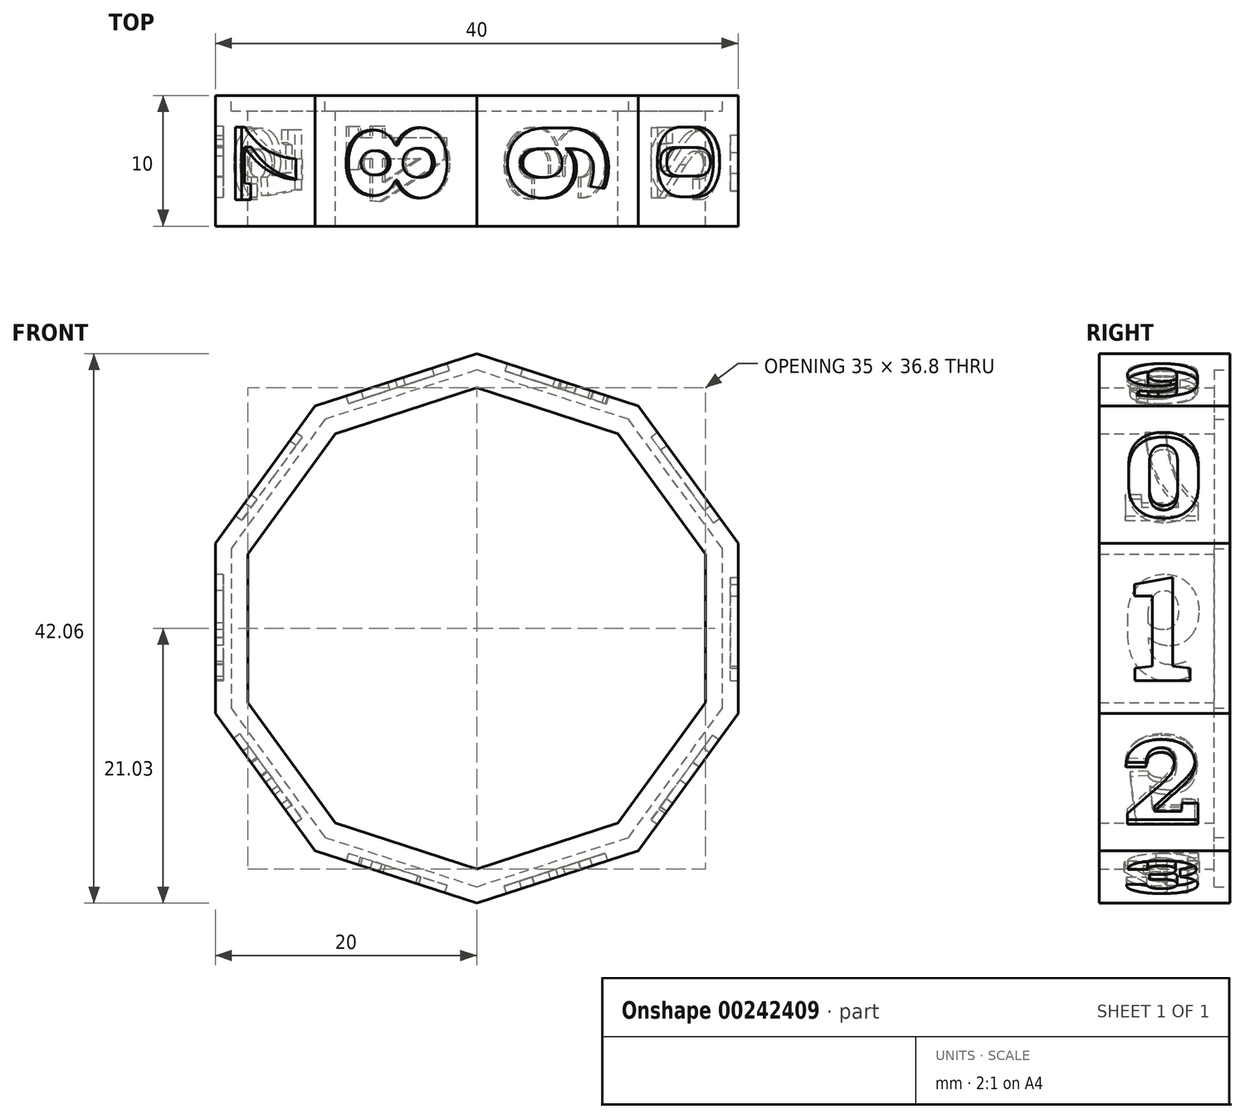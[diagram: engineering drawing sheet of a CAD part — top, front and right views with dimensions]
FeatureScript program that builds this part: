
annotation { "Feature Type Name" : "Feature", "Feature Type Description" : "" }
export const myFeature = defineFeature(function(context is Context, id is Id, definition is map)
    precondition{}
    {
        {
            var Q0;
            Q0=qCreatedBy(makeId("Front.planeOp"),FACE);
            var sketch = newSketch(context, id + "F0", { "sketchPlane" : qUnion([Q0])});
            skCircle(sketch, "E0.cCircle", {"center": v(0, 0) * mm, "radius": 20 * mm, "construction": true});
            skLineSegment(sketch, "E0.0", {"start": v(20, 6.5) * mm, "end": v(20, -6.5) * mm});
            skLineSegment(sketch, "E0.1", {"start": v(20, -6.5) * mm, "end": v(12.36, -17.01) * mm});
            skLineSegment(sketch, "E0.2", {"start": v(12.36, -17.01) * mm, "end": v(0, -21.03) * mm});
            skLineSegment(sketch, "E0.3", {"start": v(0, -21.03) * mm, "end": v(-12.36, -17.01) * mm});
            skLineSegment(sketch, "E0.4", {"start": v(-12.36, -17.01) * mm, "end": v(-20, -6.5) * mm});
            skLineSegment(sketch, "E0.5", {"start": v(-20, -6.5) * mm, "end": v(-20, 6.5) * mm});
            skLineSegment(sketch, "E0.6", {"start": v(-20, 6.5) * mm, "end": v(-12.36, 17.01) * mm});
            skLineSegment(sketch, "E0.7", {"start": v(-12.36, 17.01) * mm, "end": v(0, 21.03) * mm});
            skLineSegment(sketch, "E0.8", {"start": v(0, 21.03) * mm, "end": v(12.36, 17.01) * mm});
            skLineSegment(sketch, "E0.9", {"start": v(12.36, 17.01) * mm, "end": v(20, 6.5) * mm});
            skPoint(sketch, "E0.0.midPoint", {"position": v(20, 0) * mm});
            skSolve(sketch);
        }
        {
            var Q0;
            Q0=makeQuery(id+"F0.imprint","IMPRINT",FACE,{"disambiguationData":[TD([[makeQuery(id+"F0.imprint","IMPRINT",EDGE,{"derivedFrom":sQuery(id+"F0.wireOp",EDGE,"E0.0")}),-1.0]])]});
            extrude(context, id + "F1", {"entities" : qUnion([Q0]), "depth" : 10 * mm});
        }
        {
            var Q0;
            Q0=makeQuery(id+"F1.opExtrude","CAP_FACE",FACE,{"disambiguationData":[OSD([sQuery(id+"F0.wireOp",EDGE,"E0.0"),sQuery(id+"F0.wireOp",EDGE,"E0.1"),sQuery(id+"F0.wireOp",EDGE,"E0.2"),sQuery(id+"F0.wireOp",EDGE,"E0.3"),sQuery(id+"F0.wireOp",EDGE,"E0.4"),sQuery(id+"F0.wireOp",EDGE,"E0.5"),sQuery(id+"F0.wireOp",EDGE,"E0.6"),sQuery(id+"F0.wireOp",EDGE,"E0.7"),sQuery(id+"F0.wireOp",EDGE,"E0.8"),sQuery(id+"F0.wireOp",EDGE,"E0.9")])],"isStart":false});
            var Q1;
            Q1=makeQuery(id+"F1.opExtrude","SWEPT_BODY",BODY,{"disambiguationData":[OSD([sQuery(id+"F0.wireOp",EDGE,"E0.0"),sQuery(id+"F0.wireOp",EDGE,"E0.1"),sQuery(id+"F0.wireOp",EDGE,"E0.2"),sQuery(id+"F0.wireOp",EDGE,"E0.3"),sQuery(id+"F0.wireOp",EDGE,"E0.4"),sQuery(id+"F0.wireOp",EDGE,"E0.5"),sQuery(id+"F0.wireOp",EDGE,"E0.6"),sQuery(id+"F0.wireOp",EDGE,"E0.7"),sQuery(id+"F0.wireOp",EDGE,"E0.8"),sQuery(id+"F0.wireOp",EDGE,"E0.9")])]});
            shell(context, id + "F2", {"entities" : qUnion([Q0]), "parts" : qUnion([Q1]), "thickness" : 2.5 * mm});
        }
        {
            var Q0;
            Q0=makeQuery(id+"F2.opShell","OFFSET_FACE",FACE,{"disambiguationData":[OSD([sQuery(id+"F0.wireOp",EDGE,"E0.0"),sQuery(id+"F0.wireOp",EDGE,"E0.1"),sQuery(id+"F0.wireOp",EDGE,"E0.2"),sQuery(id+"F0.wireOp",EDGE,"E0.3"),sQuery(id+"F0.wireOp",EDGE,"E0.4"),sQuery(id+"F0.wireOp",EDGE,"E0.5"),sQuery(id+"F0.wireOp",EDGE,"E0.6"),sQuery(id+"F0.wireOp",EDGE,"E0.7"),sQuery(id+"F0.wireOp",EDGE,"E0.8"),sQuery(id+"F0.wireOp",EDGE,"E0.9")])]});
            extrude(context, id + "F3", {"entities" : qUnion([Q0]), "operationType" : NewBodyOperationType.REMOVE, "endBound" : BoundingType.THROUGH_ALL, "oppositeDirection" : true, "depth" : 25 * mm});
        }
        {
            var Q0;
            Q0=makeQuery(id+"F1.opExtrude","SWEPT_FACE",FACE,{"disambiguationData":[OSD([sQuery(id+"F0.wireOp",EDGE,"E0.0")])]});
            var sketch = newSketch(context, id + "F4", { "sketchPlane" : qUnion([Q0])});
            skText(sketch, "E1", { "text": "1", "fontName": "RobotoSlab-Bold.ttf"});
            skPoint(sketch, "E2", {"position": v(-5, 0) * mm});
            skPoint(sketch, "E3", {"position": v(-5, 6.5) * mm});
            skLineSegment(sketch, "E4", {"start": v(-5, 15.06) * mm, "end": v(-5, -15.22) * mm, "construction": true});
            skLineSegment(sketch, "E5", {"start": v(0, 0) * mm, "end": v(-19.55, 0) * mm, "construction": true});
            skPoint(sketch, "E5.endSnap0", {"position": v(-10, 0) * mm});
            const initialGuessF4  = {"E1": [-0.00764, -0.004, 1, 0, 0.008]};
            skSetInitialGuess(sketch, initialGuessF4);
            skSolve(sketch);
        }
        {
            var Q0;
            Q0=qCreatedBy(makeId("Right.planeOp"),FACE);
            var sketch = newSketch(context, id + "F5", { "sketchPlane" : qUnion([Q0])});
            skLineSegment(sketch, "E6", {"start": v(-30.34, 0) * mm, "end": v(47.05, 0) * mm, "construction": true});
            skSolve(sketch);
        }
        {
            var Q0;
            Q0=makeQuery(id+"F1.opExtrude","SWEPT_FACE",FACE,{"disambiguationData":[OSD([sQuery(id+"F0.wireOp",EDGE,"E0.1")])]});
            var sketch = newSketch(context, id + "F6", { "sketchPlane" : qUnion([Q0])});
            skText(sketch, "E7", { "text": "2", "fontName": "RobotoSlab-Bold.ttf"});
            skPoint(sketch, "E8", {"position": v(-5, 0) * mm});
            skPoint(sketch, "E9", {"position": v(-5, 6.5) * mm});
            skLineSegment(sketch, "E10", {"start": v(-5, 34.53) * mm, "end": v(-5, -39.22) * mm, "construction": true});
            const initialGuessF6  = {"E7": [-0.00823, -0.004, 1, 0, 0.008]};
            skSetInitialGuess(sketch, initialGuessF6);
            skSolve(sketch);
        }
        {
            var Q0;
            Q0=makeQuery(id+"F1.opExtrude","SWEPT_FACE",FACE,{"disambiguationData":[OSD([sQuery(id+"F0.wireOp",EDGE,"E0.2")])]});
            var sketch = newSketch(context, id + "F7", { "sketchPlane" : qUnion([Q0])});
            skText(sketch, "E11", { "text": "3", "fontName": "RobotoSlab-Bold.ttf"});
            skPoint(sketch, "E12", {"position": v(6.5, 5) * mm});
            skLineSegment(sketch, "E13", {"start": v(11.7, 5) * mm, "end": v(-11.1, 5) * mm, "construction": true});
            skPoint(sketch, "E14", {"position": v(0, 8.23) * mm});
            const initialGuessF7  = {"E11": [-0.004, 0.00823, 0, -1, 0.008]};
            skSetInitialGuess(sketch, initialGuessF7);
            skSolve(sketch);
        }
        {
            var Q0;
            Q0=makeQuery(id+"F1.opExtrude","SWEPT_FACE",FACE,{"disambiguationData":[OSD([sQuery(id+"F0.wireOp",EDGE,"E0.3")])]});
            var sketch = newSketch(context, id + "F8", { "sketchPlane" : qUnion([Q0])});
            skText(sketch, "E15", { "text": "4", "fontName": "RobotoSlab-Bold.ttf"});
            skLineSegment(sketch, "E16", {"start": v(10.7, 5) * mm, "end": v(-10.99, 5) * mm, "construction": true});
            skPoint(sketch, "E16.startSnap0", {"position": v(6.5, 5) * mm});
            skPoint(sketch, "E17", {"position": v(0, 8.32) * mm});
            const initialGuessF8  = {"E15": [-0.004, 0.00832, 0, -1, 0.008]};
            skSetInitialGuess(sketch, initialGuessF8);
            skSolve(sketch);
        }
        {
            var Q0;
            Q0=makeQuery(id+"F1.opExtrude","SWEPT_FACE",FACE,{"disambiguationData":[OSD([sQuery(id+"F0.wireOp",EDGE,"E0.4")])]});
            var sketch = newSketch(context, id + "F9", { "sketchPlane" : qUnion([Q0])});
            skText(sketch, "E18", { "text": "5", "fontName": "RobotoSlab-Bold.ttf"});
            skPoint(sketch, "E19", {"position": v(8.16, 0) * mm});
            const initialGuessF9  = {"E18": [0.00816, 0.004, -1, 0, 0.008]};
            skSetInitialGuess(sketch, initialGuessF9);
            skSolve(sketch);
        }
        {
            var Q0;
            Q0=makeQuery(id+"F1.opExtrude","SWEPT_FACE",FACE,{"disambiguationData":[OSD([sQuery(id+"F0.wireOp",EDGE,"E0.5")])]});
            var sketch = newSketch(context, id + "F10", { "sketchPlane" : qUnion([Q0])});
            skText(sketch, "E20", { "text": "6", "fontName": "RobotoSlab-Bold.ttf"});
            skPoint(sketch, "E21", {"position": v(8.33, 0) * mm});
            const initialGuessF10  = {"E20": [0.00833, 0.004, -1, 0, 0.008]};
            skSetInitialGuess(sketch, initialGuessF10);
            skSolve(sketch);
        }
        {
            var Q0;
            Q0=makeQuery(id+"F1.opExtrude","SWEPT_FACE",FACE,{"disambiguationData":[OSD([sQuery(id+"F0.wireOp",EDGE,"E0.6")])]});
            var sketch = newSketch(context, id + "F11", { "sketchPlane" : qUnion([Q0])});
            skText(sketch, "E22", { "text": "7", "fontName": "RobotoSlab-Bold.ttf"});
            skPoint(sketch, "E23", {"position": v(8.26, 0) * mm});
            const initialGuessF11  = {"E22": [0.00826, 0.004, -1, 0, 0.008]};
            skSetInitialGuess(sketch, initialGuessF11);
            skSolve(sketch);
        }
        {
            var Q0;
            Q0=makeQuery(id+"F1.opExtrude","SWEPT_FACE",FACE,{"disambiguationData":[OSD([sQuery(id+"F0.wireOp",EDGE,"E0.7")])]});
            var sketch = newSketch(context, id + "F12", { "sketchPlane" : qUnion([Q0])});
            skText(sketch, "E24", { "text": "8", "fontName": "RobotoSlab-Bold.ttf"});
            skPoint(sketch, "E25", {"position": v(0, -8.21) * mm});
            const initialGuessF12  = {"E24": [0.004, -0.00821, 0, 1, 0.008]};
            skSetInitialGuess(sketch, initialGuessF12);
            skSolve(sketch);
        }
        {
            var Q0;
            Q0=makeQuery(id+"F1.opExtrude","SWEPT_FACE",FACE,{"disambiguationData":[OSD([sQuery(id+"F0.wireOp",EDGE,"E0.8")])]});
            var sketch = newSketch(context, id + "F13", { "sketchPlane" : qUnion([Q0])});
            skText(sketch, "E26", { "text": "9", "fontName": "RobotoSlab-Bold.ttf"});
            skPoint(sketch, "E27", {"position": v(0, -1.8) * mm});
            const initialGuessF13  = {"E26": [0.004, -0.0082, 0, 1, 0.008]};
            skSetInitialGuess(sketch, initialGuessF13);
            skSolve(sketch);
        }
        {
            var Q0;
            Q0=makeQuery(id+"F1.opExtrude","SWEPT_FACE",FACE,{"disambiguationData":[OSD([sQuery(id+"F0.wireOp",EDGE,"E0.9")])]});
            var sketch = newSketch(context, id + "F14", { "sketchPlane" : qUnion([Q0])});
            skText(sketch, "E28", { "text": "0", "fontName": "RobotoSlab-Bold.ttf"});
            skPoint(sketch, "E29", {"position": v(-8.28, 0) * mm});
            const initialGuessF14  = {"E28": [-0.00828, -0.004, 1, 0, 0.008]};
            skSetInitialGuess(sketch, initialGuessF14);
            skSolve(sketch);
        }
        {
            var Q0;
            Q0=makeQuery(id+"F0.imprint","IMPRINT",FACE,{"disambiguationData":[TD([[makeQuery(id+"F0.imprint","IMPRINT",EDGE,{"derivedFrom":sQuery(id+"F0.wireOp",EDGE,"E0.0")}),-1.0]])]});
            var sketch = newSketch(context, id + "F15", { "sketchPlane" : qUnion([Q0])});
            skLineSegment(sketch, "E30.0", {"start": v(18.8, 6.1) * mm, "end": v(11.62, 16) * mm});
            skLineSegment(sketch, "E30.1", {"start": v(18.8, -6.1) * mm, "end": v(18.8, 6.1) * mm});
            skLineSegment(sketch, "E30.2", {"start": v(11.62, 16) * mm, "end": v(0, 19.77) * mm});
            skLineSegment(sketch, "E30.3", {"start": v(11.62, -16) * mm, "end": v(18.8, -6.1) * mm});
            skLineSegment(sketch, "E30.4", {"start": v(0, -19.77) * mm, "end": v(11.62, -16) * mm});
            skLineSegment(sketch, "E30.5", {"start": v(-11.62, -16) * mm, "end": v(0, -19.77) * mm});
            skLineSegment(sketch, "E30.6", {"start": v(0, 19.77) * mm, "end": v(-11.62, 16) * mm});
            skLineSegment(sketch, "E30.7", {"start": v(-11.62, 16) * mm, "end": v(-18.8, 6.1) * mm});
            skLineSegment(sketch, "E30.8", {"start": v(-18.8, 6.1) * mm, "end": v(-18.8, -6.1) * mm});
            skLineSegment(sketch, "E30.9", {"start": v(-18.8, -6.1) * mm, "end": v(-11.62, -16) * mm});
            skLineSegment(sketch, "E31.0", {"start": v(13.8, 4.48) * mm, "end": v(8.53, 11.74) * mm});
            skLineSegment(sketch, "E31.1", {"start": v(13.8, -4.48) * mm, "end": v(13.8, 4.48) * mm});
            skLineSegment(sketch, "E31.2", {"start": v(8.53, 11.74) * mm, "end": v(0, 14.51) * mm});
            skLineSegment(sketch, "E31.3", {"start": v(8.53, -11.74) * mm, "end": v(13.8, -4.48) * mm});
            skLineSegment(sketch, "E31.4", {"start": v(0, -14.51) * mm, "end": v(8.53, -11.74) * mm});
            skLineSegment(sketch, "E31.5", {"start": v(-8.53, -11.74) * mm, "end": v(0, -14.51) * mm});
            skLineSegment(sketch, "E31.6", {"start": v(0, 14.51) * mm, "end": v(-8.53, 11.74) * mm});
            skLineSegment(sketch, "E31.7", {"start": v(-8.53, 11.74) * mm, "end": v(-13.8, 4.48) * mm});
            skLineSegment(sketch, "E31.8", {"start": v(-13.8, 4.48) * mm, "end": v(-13.8, -4.48) * mm});
            skLineSegment(sketch, "E31.9", {"start": v(-13.8, -4.48) * mm, "end": v(-8.53, -11.74) * mm});
            skSolve(sketch);
        }
        {
            var Q0;
            Q0=qSketchRegion(id+"F6",true);
            extrude(context, id + "F16", {"entities" : qUnion([Q0]), "operationType" : NewBodyOperationType.REMOVE, "oppositeDirection" : true, "depth" : 0.6 * mm});
        }
        {
            var Q0;
            Q0=qSketchRegion(id+"F12",true);
            extrude(context, id + "F17", {"entities" : qUnion([Q0]), "operationType" : NewBodyOperationType.REMOVE, "oppositeDirection" : true, "depth" : 0.6 * mm});
        }
        {
            var Q0;
            Q0=qSketchRegion(id+"F11",true);
            extrude(context, id + "F18", {"entities" : qUnion([Q0]), "operationType" : NewBodyOperationType.REMOVE, "oppositeDirection" : true, "depth" : 0.6 * mm});
        }
        {
            var Q0;
            Q0=qSketchRegion(id+"F4",true);
            extrude(context, id + "F19", {"entities" : qUnion([Q0]), "operationType" : NewBodyOperationType.REMOVE, "oppositeDirection" : true, "depth" : 0.6 * mm});
        }
        {
            var Q0;
            Q0=qSketchRegion(id+"F7",true);
            extrude(context, id + "F20", {"entities" : qUnion([Q0]), "operationType" : NewBodyOperationType.REMOVE, "oppositeDirection" : true, "depth" : 0.6 * mm});
        }
        {
            var Q0;
            Q0=qSketchRegion(id+"F9",true);
            extrude(context, id + "F21", {"entities" : qUnion([Q0]), "operationType" : NewBodyOperationType.REMOVE, "oppositeDirection" : true, "depth" : 0.6 * mm});
        }
        {
            var Q0;
            Q0=qSketchRegion(id+"F8",true);
            extrude(context, id + "F22", {"entities" : qUnion([Q0]), "operationType" : NewBodyOperationType.REMOVE, "oppositeDirection" : true, "depth" : 0.6 * mm});
        }
        {
            var Q0;
            Q0=qSketchRegion(id+"F10",true);
            extrude(context, id + "F23", {"entities" : qUnion([Q0]), "operationType" : NewBodyOperationType.REMOVE, "oppositeDirection" : true, "depth" : 0.6 * mm});
        }
        {
            var Q0;
            Q0=qSketchRegion(id+"F13",true);
            extrude(context, id + "F24", {"entities" : qUnion([Q0]), "operationType" : NewBodyOperationType.REMOVE, "oppositeDirection" : true, "depth" : 0.6 * mm});
        }
        {
            var Q0;
            Q0=qSketchRegion(id+"F14",true);
            extrude(context, id + "F25", {"entities" : qUnion([Q0]), "operationType" : NewBodyOperationType.REMOVE, "oppositeDirection" : true, "depth" : 0.6 * mm});
        }
        {
            var Q0;
            Q0=makeQuery(id+"F15.imprint","IMPRINT",FACE,{"disambiguationData":[TD([[makeQuery(id+"F15.imprint","IMPRINT",EDGE,{"derivedFrom":sQuery(id+"F15.wireOp",EDGE,"E30.0")}),1.0]])]});
            extrude(context, id + "F26", {"entities" : qUnion([Q0]), "operationType" : NewBodyOperationType.REMOVE, "depth" : 1.2 * mm});
        }
    });
